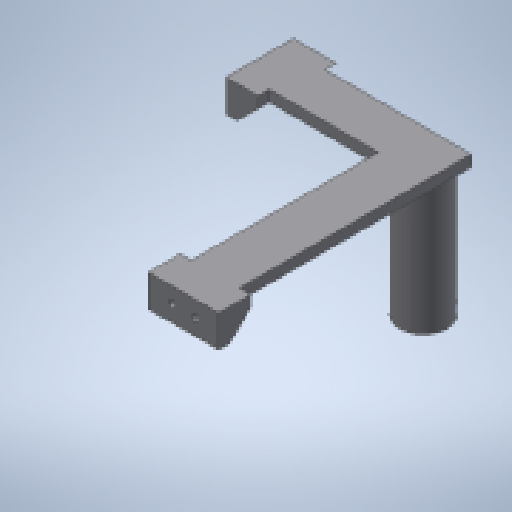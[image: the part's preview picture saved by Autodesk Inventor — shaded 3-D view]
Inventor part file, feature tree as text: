
AUTODESK INVENTOR PART (.ipt)
format: ipt  version: 2023 (Build 270158000, 158)  size: 284,672 bytes
history: native  units: mm
features: extrude x13, sketch x13, other x3, projected_geometry x2, reference x1
ambient origin geometry x8: Origin, YZ Plane, XZ Plane, XY Plane, X Axis, Y Axis, Z Axis, Center Point
bodies: Solid1 (feature_tree)
feature tree (32):
  extrude  "Extrusion1"  Depth=20.0mm
  extrude  "Extrusion2"  Depth=150.0mm
  sketch  "Sketch3"  dims[d4=30.0mm d5=0.0mm d6=80.0mm d7=7.0mm d8=0.0mm d9=0.0mm]
  extrude  "Extrusion3"  Depth=80.0mm TaperAngle=0.0deg
  extrude  "Extrusion4"  Depth=10.0mm
  extrude  "Extrusion5"  Depth=10.0mm
  extrude  "Extrusion6"  Depth=15.0mm
  extrude  "Extrusion7"  Depth=7.0mm TaperAngle=0.0deg
  extrude  "Extrusion8"  Depth=7.0mm TaperAngle=0.0deg
  extrude  "Extrusion9"  Depth=11.0mm
  extrude  "Extrusion10"  Depth=80.0mm
  extrude  "Extrusion11"  Depth=7.0mm TaperAngle=0.0deg
  extrude  "Extrusion12"  Depth=15.0mm
  extrude  "Extrusion13"  Depth=7.0mm TaperAngle=0.0deg
  sketch  "Sketch1"  dims[d0=7.0mm d1=20.0mm]
  sketch  "Sketch2"  dims[d2=7.0mm d3=150.0mm]
  sketch  "Sketch4"  dims[d10=10.0mm d11=4.5mm]
  projected_geometry  "Projected Loop1"
  sketch  "Sketch5"  dims[d12=4.5mm d13=10.0mm]
  projected_geometry  "Projected Loop2"
  sketch  "Sketch6"  dims[d14=15.0mm d15=7.5mm]
  sketch  "Sketch7"  dims[d16=13.0mm d17=7.0mm d18=0.0mm]
  sketch  "Sketch8"  dims[d19=7.0mm d20=0.0mm d21=7.0mm d22=0.0mm]
  reference  "Reference1"
  sketch  "Sketch9"  dims[d23=11.0mm d24=11.0mm]
  sketch  "Sketch10"  dims[d25=12.0mm d26=0.0mm d27=80.0mm]
  sketch  "Sketch11"  dims[d28=7.0mm d29=72.0mm d30=0.0mm]
  sketch  "Sketch13"  dims[d31=0.0mm d32=15.0mm]
  sketch  "Sketch15"  dims[d33=20.0mm d34=7.0mm d35=0.0mm d36=7.0mm d37=0.0mm d38=7.0mm d39=7.0mm d40=13.0mm d41=7.0mm d42=0.0mm d43=0.0mm d44=45.0deg d45=7.0mm d46=0.0mm d47=7.0mm d48=0.0mm d49=10.0mm d50=10.0mm d51=15.0mm d52=6.5mm d53=6.507214mm d54=4.5mm d55=4.5mm d56=7.0mm d57=0.0mm d58=10.0mm d59=10.0mm d60=20.0mm d61=0.0mm]
  other  "<userpath>\OneDrive\ClawdDrive\Objet3D\3DPrinter\inventor\3DPrinterBeltCoreXY.iam"
  other  "3DPrinterBeltCoreXY.iam"
  other  "20X20 - T-slot - Vertical:2"
